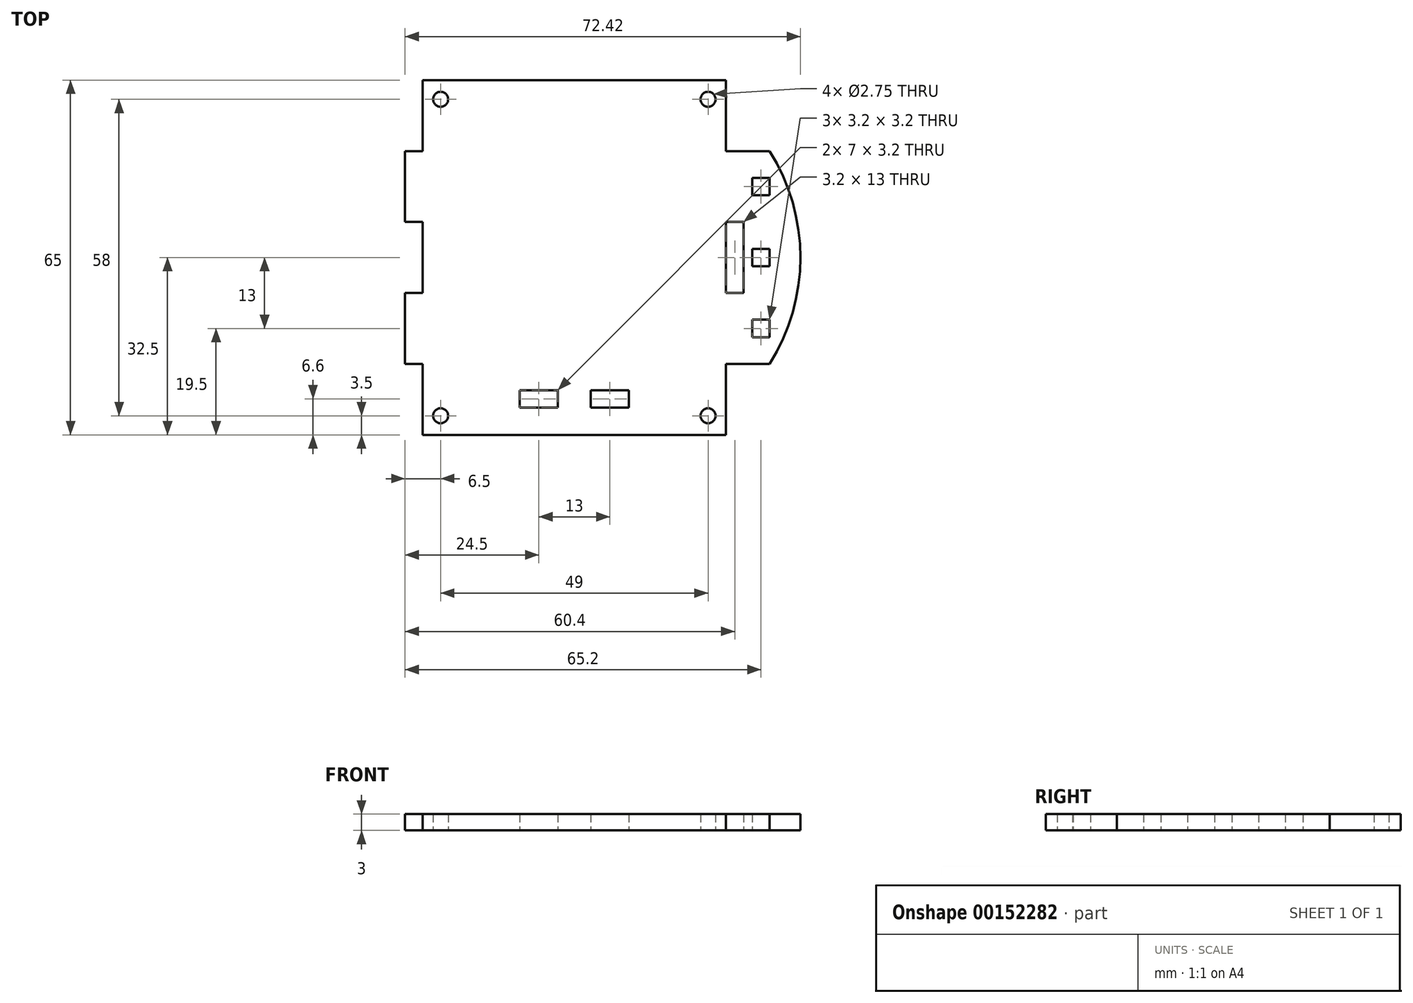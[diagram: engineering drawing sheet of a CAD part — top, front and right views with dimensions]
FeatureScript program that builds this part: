
annotation { "Feature Type Name" : "Feature", "Feature Type Description" : "" }
export const myFeature = defineFeature(function(context is Context, id is Id, definition is map)
    precondition{}
    {
        {
            var Q0;
            Q0=qCreatedBy(makeId("Top.planeOp"),FACE);
            var sketch = newSketch(context, id + "F0", { "sketchPlane" : qUnion([Q0])});
            skLineSegment(sketch, "E0.bottom", {"start": v(27.8, -32.5) * mm, "end": v(-27.8, -32.5) * mm});
            skLineSegment(sketch, "E0.top", {"start": v(27.8, 32.5) * mm, "end": v(-27.8, 32.5) * mm});
            skPoint(sketch, "E0.middle", {"position": v(0, 0) * mm});
            skLineSegment(sketch, "E1", {"start": v(-27.8, -32.5) * mm, "end": v(-27.8, -19.5) * mm});
            skLineSegment(sketch, "E2", {"start": v(-27.8, -19.5) * mm, "end": v(-31, -19.5) * mm});
            skLineSegment(sketch, "E3", {"start": v(-31, -6.5) * mm, "end": v(-27.8, -6.5) * mm});
            skLineSegment(sketch, "E4", {"start": v(-27.8, -6.5) * mm, "end": v(-27.8, 6.5) * mm});
            skLineSegment(sketch, "E5", {"start": v(-27.8, 6.5) * mm, "end": v(-31, 6.5) * mm});
            skLineSegment(sketch, "E6", {"start": v(0, 0) * mm, "end": v(0, -32.5) * mm, "construction": true});
            skCircle(sketch, "E7", {"center": v(24.5, -29) * mm, "radius": 1.38 * mm});
            skCircle(sketch, "E8.MirrorC", {"center": v(-24.5, -29) * mm, "radius": 1.38 * mm});
            skCircle(sketch, "E9", {"center": v(-24.5, 29) * mm, "radius": 1.38 * mm});
            skCircle(sketch, "E10.MirrorC", {"center": v(24.5, 29) * mm, "radius": 1.38 * mm});
            skLineSegment(sketch, "E11", {"start": v(31, 6.5) * mm, "end": v(27.8, 6.5) * mm});
            skLineSegment(sketch, "E12", {"start": v(27.8, 6.5) * mm, "end": v(27.8, -6.5) * mm});
            skLineSegment(sketch, "E13", {"start": v(27.8, -6.5) * mm, "end": v(31, -6.5) * mm});
            skLineSegment(sketch, "E14", {"start": v(31, -19.5) * mm, "end": v(27.8, -19.5) * mm});
            skLineSegment(sketch, "E15", {"start": v(27.8, -19.5) * mm, "end": v(27.8, -32.5) * mm});
            skLineSegment(sketch, "E16", {"start": v(-27.8, -32.5) * mm, "end": v(0, -32.5) * mm, "construction": true});
            skLineSegment(sketch, "E17", {"start": v(0, -32.5) * mm, "end": v(0, 32.5) * mm, "construction": true});
            skLineSegment(sketch, "E18", {"start": v(0, 0) * mm, "end": v(-27.8, 0) * mm, "construction": true});
            skLineSegment(sketch, "E19", {"start": v(0, 0) * mm, "end": v(27.8, 0) * mm, "construction": true});
            skLineSegment(sketch, "E20", {"start": v(27.8, -32.5) * mm, "end": v(0, -32.5) * mm, "construction": true});
            skLineSegment(sketch, "E21", {"start": v(-27.8, -19.5) * mm, "end": v(-27.8, 32.5) * mm, "construction": true});
            skLineSegment(sketch, "E22", {"start": v(27.8, -32.5) * mm, "end": v(27.8, 32.5) * mm, "construction": true});
            skLineSegment(sketch, "E23", {"start": v(-27.8, 32.5) * mm, "end": v(-27.8, 19.5) * mm});
            skLineSegment(sketch, "E24", {"start": v(-27.8, 19.5) * mm, "end": v(-31, 19.5) * mm});
            skLineSegment(sketch, "E25", {"start": v(-31, 6.5) * mm, "end": v(-27.8, 6.5) * mm});
            skLineSegment(sketch, "E26", {"start": v(27.8, 32.5) * mm, "end": v(27.8, 19.5) * mm});
            skLineSegment(sketch, "E27", {"start": v(27.8, 19.5) * mm, "end": v(31, 19.5) * mm});
            skLineSegment(sketch, "E28", {"start": v(-31, 19.5) * mm, "end": v(-31, 6.5) * mm});
            skLineSegment(sketch, "E29", {"start": v(-31, -6.5) * mm, "end": v(-31, -19.5) * mm});
            skLineSegment(sketch, "E30", {"start": v(-31, 19.5) * mm, "end": v(-31, 36.27) * mm, "construction": true});
            skLineSegment(sketch, "E31", {"start": v(31, -19.5) * mm, "end": v(35.8, -19.5) * mm});
            skLineSegment(sketch, "E32", {"start": v(35.8, 19.5) * mm, "end": v(31, 19.5) * mm});
            skLineSegment(sketch, "E33", {"start": v(34.2, -6.5) * mm, "end": v(34.2, -19.5) * mm, "construction": true});
            skLineSegment(sketch, "E34", {"start": v(31, -13) * mm, "end": v(37.4, -13) * mm, "construction": true});
            skLineSegment(sketch, "E35.bottom", {"start": v(35.8, -11.4) * mm, "end": v(32.6, -11.4) * mm});
            skLineSegment(sketch, "E35.top", {"start": v(35.8, -14.6) * mm, "end": v(32.6, -14.6) * mm});
            skLineSegment(sketch, "E35.left", {"start": v(35.8, -11.4) * mm, "end": v(35.8, -14.6) * mm});
            skLineSegment(sketch, "E35.right", {"start": v(32.6, -11.4) * mm, "end": v(32.6, -14.6) * mm});
            skPoint(sketch, "E35.middle", {"position": v(34.2, -13) * mm});
            skLineSegment(sketch, "E36", {"start": v(31, 13) * mm, "end": v(37.4, 13) * mm, "construction": true});
            skLineSegment(sketch, "E37", {"start": v(34.2, 19.5) * mm, "end": v(34.2, 6.5) * mm, "construction": true});
            skLineSegment(sketch, "E38.bottom", {"start": v(35.8, 14.6) * mm, "end": v(32.6, 14.6) * mm});
            skLineSegment(sketch, "E38.top", {"start": v(35.8, 11.4) * mm, "end": v(32.6, 11.4) * mm});
            skLineSegment(sketch, "E38.left", {"start": v(35.8, 14.6) * mm, "end": v(35.8, 11.4) * mm});
            skLineSegment(sketch, "E38.right", {"start": v(32.6, 14.6) * mm, "end": v(32.6, 11.4) * mm});
            skPoint(sketch, "E38.middle", {"position": v(34.2, 13) * mm});
            skLineSegment(sketch, "E39", {"start": v(31, 6.5) * mm, "end": v(31, -6.5) * mm});
            skLineSegment(sketch, "E40", {"start": v(32.6, 11.4) * mm, "end": v(32.6, -11.4) * mm, "construction": true});
            skLineSegment(sketch, "E41", {"start": v(32.6, 0) * mm, "end": v(4.8, 0) * mm, "construction": true});
            skArc(sketch, "E42", {"start": v(35.8, -19.5) * mm, "mid": v(41.42, 0) * mm, "end": v(35.8, 19.5) * mm});
            skPoint(sketch, "E43.orphan", {"position": v(37.4, -6.5) * mm});
            skPoint(sketch, "E44.orphan", {"position": v(37.4, 6.5) * mm});
            skLineSegment(sketch, "E45", {"start": v(34.2, 6.5) * mm, "end": v(34.2, -6.5) * mm, "construction": true});
            skLineSegment(sketch, "E46", {"start": v(34.2, 0) * mm, "end": v(34.2, 1.6) * mm, "construction": true});
            skLineSegment(sketch, "E47", {"start": v(34.2, 1.6) * mm, "end": v(35.8, 1.6) * mm});
            skLineSegment(sketch, "E48", {"start": v(35.8, 1.6) * mm, "end": v(35.8, -1.6) * mm});
            skLineSegment(sketch, "E49", {"start": v(35.8, -1.6) * mm, "end": v(32.6, -1.6) * mm});
            skLineSegment(sketch, "E50", {"start": v(32.6, -1.6) * mm, "end": v(32.6, 1.6) * mm});
            skLineSegment(sketch, "E51", {"start": v(32.6, 1.6) * mm, "end": v(34.2, 1.6) * mm});
            skLineSegment(sketch, "E52", {"start": v(-24.5, 29) * mm, "end": v(0, 29) * mm, "construction": true});
            skLineSegment(sketch, "E53", {"start": v(0, 29) * mm, "end": v(0, -24.3) * mm, "construction": true});
            skLineSegment(sketch, "E54", {"start": v(0, -24.3) * mm, "end": v(3, -24.3) * mm, "construction": true});
            skLineSegment(sketch, "E55", {"start": v(3, -24.3) * mm, "end": v(-3, -24.3) * mm, "construction": true});
            skLineSegment(sketch, "E56.bottom", {"start": v(-3, -24.3) * mm, "end": v(-10, -24.3) * mm});
            skLineSegment(sketch, "E56.top", {"start": v(-3, -27.5) * mm, "end": v(-10, -27.5) * mm});
            skLineSegment(sketch, "E56.left", {"start": v(-3, -24.3) * mm, "end": v(-3, -27.5) * mm});
            skLineSegment(sketch, "E56.right", {"start": v(-10, -24.3) * mm, "end": v(-10, -27.5) * mm});
            skLineSegment(sketch, "E57.bottom", {"start": v(3, -24.3) * mm, "end": v(10, -24.3) * mm});
            skLineSegment(sketch, "E57.top", {"start": v(3, -27.5) * mm, "end": v(10, -27.5) * mm});
            skLineSegment(sketch, "E57.left", {"start": v(3, -24.3) * mm, "end": v(3, -27.5) * mm});
            skLineSegment(sketch, "E57.right", {"start": v(10, -24.3) * mm, "end": v(10, -27.5) * mm});
            skSolve(sketch);
        }
        {
            var Q0;
            Q0=qSketchRegion(id+"F0",true);
            extrude(context, id + "F1", {"entities" : qUnion([Q0]), "endBound" : BoundingType.SYMMETRIC, "depth" : 3 * mm});
        }
    });
